# Revit family: БДС
name_source: partatom
category: Устройства вызова и оповещения
revit_build: Autodesk Revit 2017 (Build: 20160225_1515(x64)
units: mm (PartAtom-declared; Revit-internal decimal feet)

## family parameters
Всегда вертикально = Да
На основе рабочей плоскости = Нет
Общий = Нет
При загрузке вырезать с полостями = Нет
Размер круглого соединителя = Использовать диаметр
Сохранять ориентацию аннотаций = Нет
Тип детали = Нормальный
Точка расчета площади = Нет

## types (1)
- БДС
    URL = http://rechor.ru
    Высота = 90 мм
    Глубина = 430 мм
    Изготовитель = СОУЭ 'Речор'
    Материал корпуса = Сталь, порошковая
    Мощность = 45 Вт
    Описание = Блок диспетчерской связи БДС на тридцать абонентов, предназначен для обеспечения двухсторонней цифровой дуплексной связи зон пожарного оповещения с помещением пожарного поста или диспетчерской. Конструктивно БДС выполнен в виде функционально законченного блока, рассчитанного на установку в стойку 19” или на стол.
    Ширина = 490 мм
